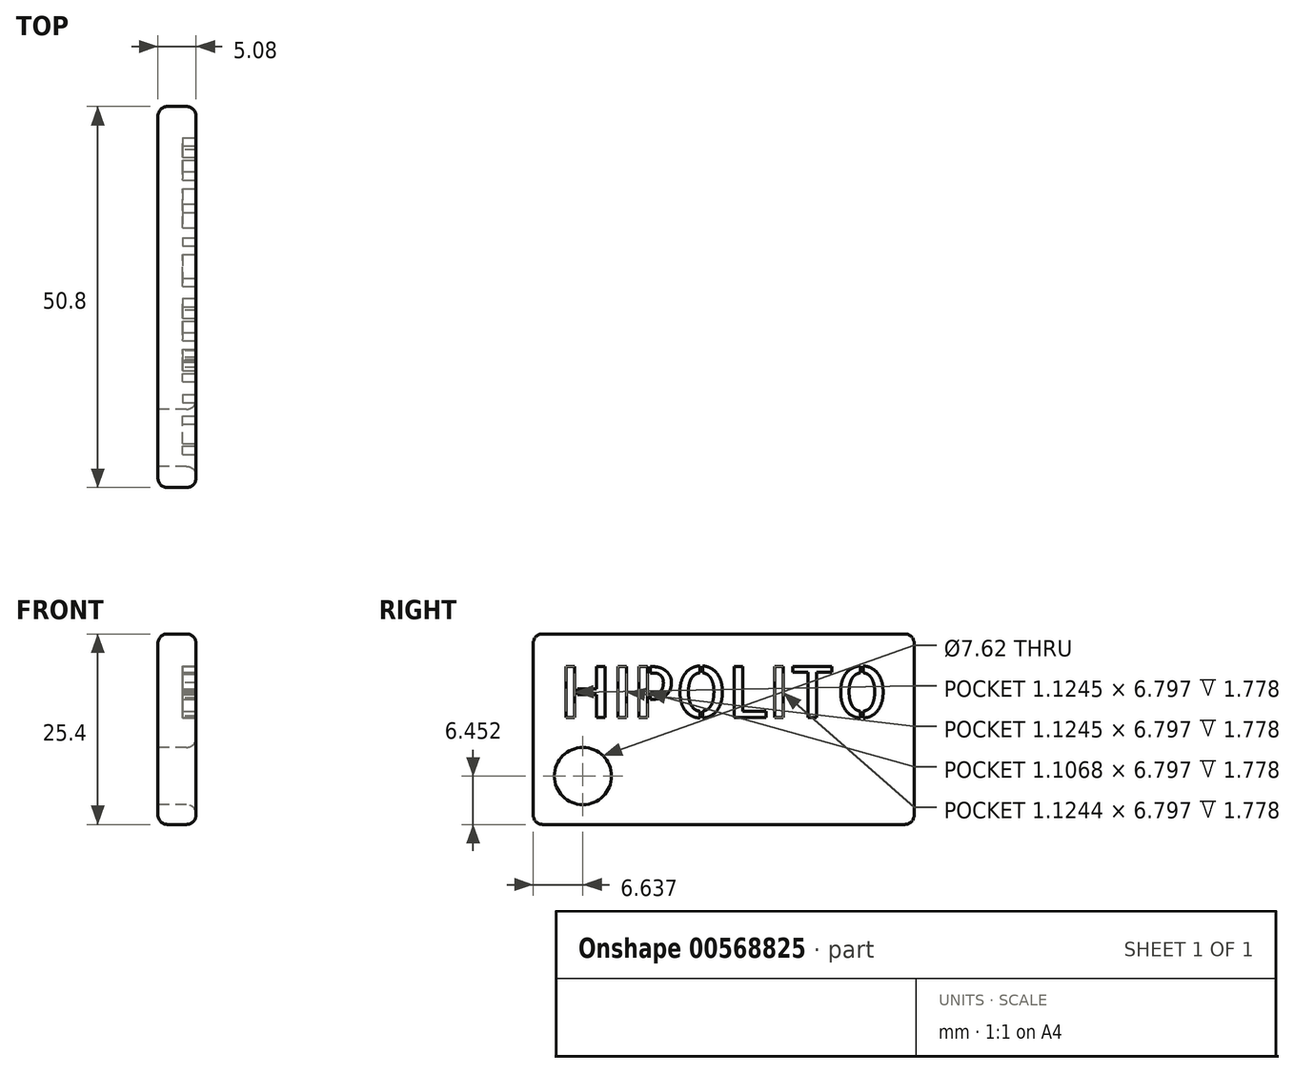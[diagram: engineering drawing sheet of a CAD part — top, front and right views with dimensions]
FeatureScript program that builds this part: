
annotation { "Feature Type Name" : "Feature", "Feature Type Description" : "" }
export const myFeature = defineFeature(function(context is Context, id is Id, definition is map)
    precondition{}
    {
        {
            var Q0;
            Q0=qCreatedBy(makeId("Right.planeOp"),FACE);
            var sketch = newSketch(context, id + "F0", { "sketchPlane" : qUnion([Q0])});
            skLineSegment(sketch, "E0.bottom", {"start": v(0, 0) * mm, "end": v(50.8, 0) * mm});
            skLineSegment(sketch, "E0.top", {"start": v(0, 25.4) * mm, "end": v(50.8, 25.4) * mm});
            skLineSegment(sketch, "E0.left", {"start": v(0, 0) * mm, "end": v(0, 25.4) * mm});
            skLineSegment(sketch, "E0.right", {"start": v(50.8, 0) * mm, "end": v(50.8, 25.4) * mm});
            skCircle(sketch, "E1", {"center": v(6.64, 6.45) * mm, "radius": 3.69 * mm});
            skCircle(sketch, "E2", {"center": v(6.64, 6.45) * mm, "radius": 3.81 * mm});
            skSolve(sketch);
        }
        {
            var Q0;
            Q0=makeQuery(id+"F0.imprint","IMPRINT",FACE,{"disambiguationData":[TD([[makeQuery(id+"F0.imprint","IMPRINT",EDGE,{"derivedFrom":sQuery(id+"F0.wireOp",EDGE,"E0.bottom")}),1.0]])]});
            extrude(context, id + "F1", {"entities" : qUnion([Q0]), "depth" : 5.08 * mm, "offsetDistance" : 25.4 * mm});
        }
        {
            var Q0;
            Q0=makeQuery(id+"F1.opExtrude","CAP_EDGE",EDGE,{"disambiguationData":[OSD([sQuery(id+"F0.wireOp",EDGE,"E0.top")])],"isStart":false});
            var Q1;
            Q1=makeQuery(id+"F1.opExtrude","CAP_FACE",FACE,{"disambiguationData":[OSD([sQuery(id+"F0.wireOp",EDGE,"E0.bottom"),sQuery(id+"F0.wireOp",EDGE,"E0.top"),sQuery(id+"F0.wireOp",EDGE,"E0.left"),sQuery(id+"F0.wireOp",EDGE,"E0.right"),sQuery(id+"F0.wireOp",EDGE,"E2")])],"isStart":false});
            var Q2;
            Q2=makeQuery(id+"F1.opExtrude","SWEPT_EDGE",EDGE,{"disambiguationData":[OSD([sQuery(id+"F0.wireOp",EDGE,"E0.bottom"),sQuery(id+"F0.wireOp",EDGE,"E0.left")])]});
            var Q3;
            Q3=makeQuery(id+"F1.opExtrude","SWEPT_EDGE",EDGE,{"disambiguationData":[OSD([sQuery(id+"F0.wireOp",EDGE,"E0.top"),sQuery(id+"F0.wireOp",EDGE,"E0.left")])]});
            var Q4;
            Q4=makeQuery(id+"F1.opExtrude","CAP_EDGE",EDGE,{"disambiguationData":[OSD([sQuery(id+"F0.wireOp",EDGE,"E0.left")])],"isStart":true});
            var Q5;
            Q5=makeQuery(id+"F1.opExtrude","CAP_EDGE",EDGE,{"disambiguationData":[OSD([sQuery(id+"F0.wireOp",EDGE,"E0.right")])],"isStart":true});
            var Q6;
            Q6=makeQuery(id+"F1.opExtrude","CAP_EDGE",EDGE,{"disambiguationData":[OSD([sQuery(id+"F0.wireOp",EDGE,"E0.bottom")])],"isStart":true});
            var Q7;
            Q7=makeQuery(id+"F1.opExtrude","CAP_EDGE",EDGE,{"disambiguationData":[OSD([sQuery(id+"F0.wireOp",EDGE,"E0.top")])],"isStart":true});
            var Q8;
            Q8=makeQuery(id+"F1.opExtrude","SWEPT_FACE",FACE,{"disambiguationData":[OSD([sQuery(id+"F0.wireOp",EDGE,"E0.right")])]});
            fillet(context, id + "F2", {"entities" : qUnion([Q0, Q1, Q2, Q3, Q4, Q5, Q6, Q7, Q8]), "radius" : 1.27 * mm, "tangentPropagation" : true, "allowEdgeOverflow" : false});
        }
        {
            var Q0;
            Q0=makeQuery(id+"F1.opExtrude","CAP_FACE",FACE,{"disambiguationData":[OSD([sQuery(id+"F0.wireOp",EDGE,"E0.bottom"),sQuery(id+"F0.wireOp",EDGE,"E0.top"),sQuery(id+"F0.wireOp",EDGE,"E0.left"),sQuery(id+"F0.wireOp",EDGE,"E0.right"),sQuery(id+"F0.wireOp",EDGE,"E2")])],"isStart":false});
            var sketch = newSketch(context, id + "F3", { "sketchPlane" : qUnion([Q0])});
            skText(sketch, "E3", { "text": "HIPOLITO", "fontName": "AllertaStencil-Regular.ttf"});
            const initialGuessF3  = {"E3": [0.00353, 0.01423, 1, 0, 0.0068]};
            skSetInitialGuess(sketch, initialGuessF3);
            skSolve(sketch);
        }
        {
            var Q0;
            Q0 = qSketchRegion(id + "F3", true);
            extrude(context, id + "F4", {"entities" : qUnion([Q0]), "operationType" : NewBodyOperationType.REMOVE, "oppositeDirection" : true, "depth" : 1.78 * mm, "offsetDistance" : 25.4 * mm});
        }
    });
